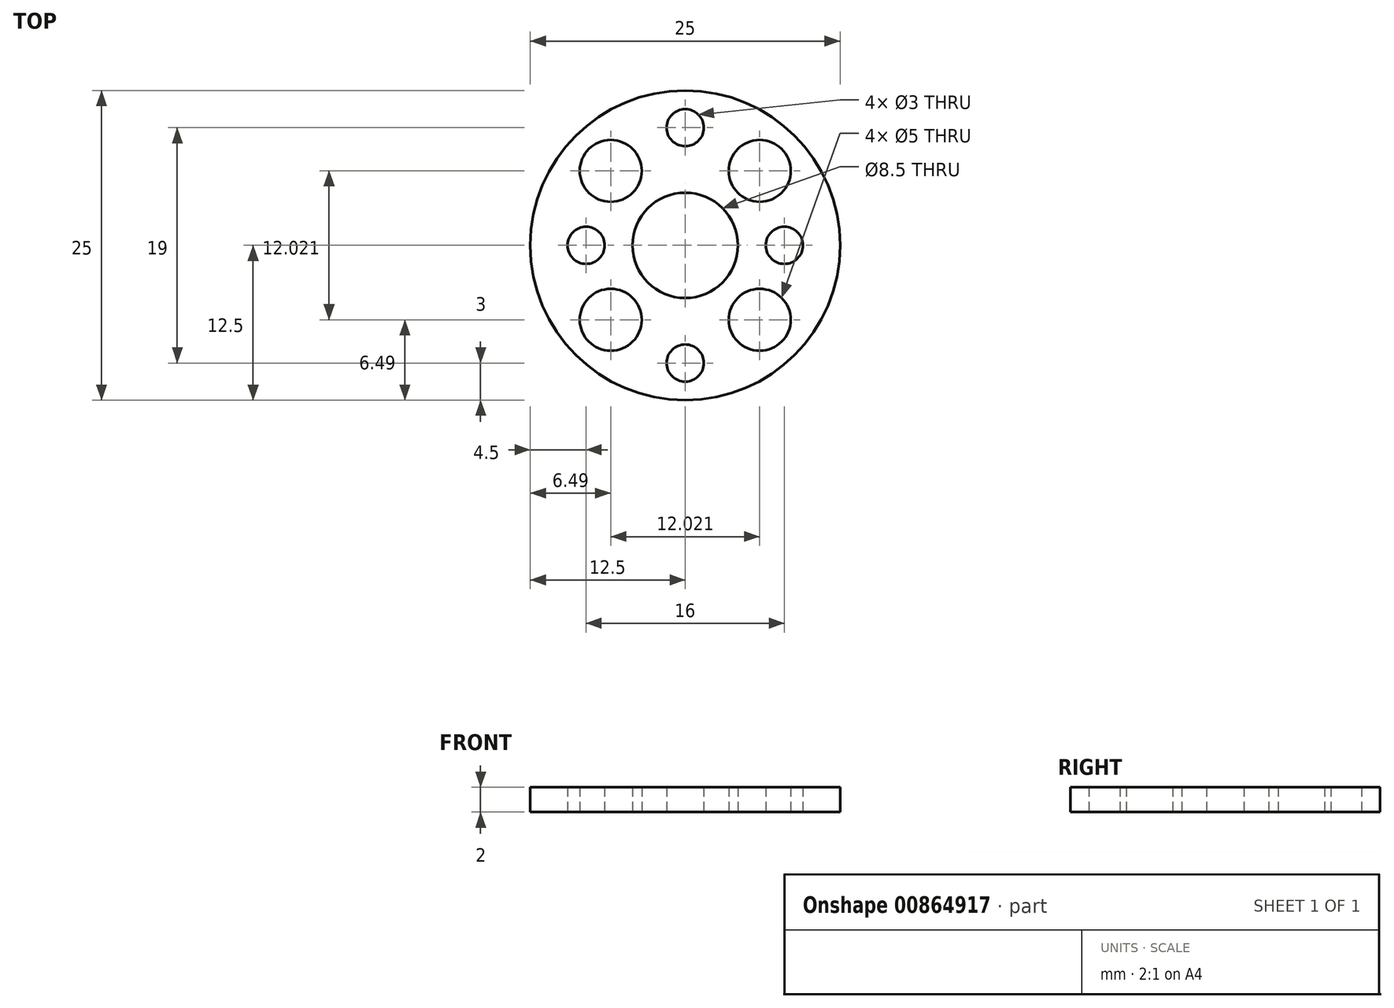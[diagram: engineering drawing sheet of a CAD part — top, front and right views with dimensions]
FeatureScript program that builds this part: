
annotation { "Feature Type Name" : "Feature", "Feature Type Description" : "" }
export const myFeature = defineFeature(function(context is Context, id is Id, definition is map)
    precondition{}
    {
        {
            var Q0;
            Q0=qCreatedBy(makeId("Top.planeOp"),FACE);
            var sketch = newSketch(context, id + "F0", { "sketchPlane" : qUnion([Q0])});
            skCircle(sketch, "E0", {"center": v(0, 0) * mm, "radius": 12.5 * mm});
            skCircle(sketch, "E1", {"center": v(0, 0) * mm, "radius": 4.25 * mm});
            skCircle(sketch, "E2", {"center": v(0, 9.5) * mm, "radius": 1.5 * mm});
            skCircle(sketch, "E3.2.0", {"center": v(0, -9.5) * mm, "radius": 1.5 * mm});
            skLineSegment(sketch, "E3.anchor1", {"start": v(0, 0) * mm, "end": v(0, 9.5) * mm, "construction": true});
            skLineSegment(sketch, "E3.anchor2", {"start": v(0, 0) * mm, "end": v(0, -9.5) * mm, "construction": true});
            skCircle(sketch, "E4", {"center": v(8, 0) * mm, "radius": 1.5 * mm});
            skCircle(sketch, "E5.2.0", {"center": v(-8, 0) * mm, "radius": 1.5 * mm});
            skLineSegment(sketch, "E5.anchor1", {"start": v(0, 0) * mm, "end": v(8, 0) * mm, "construction": true});
            skLineSegment(sketch, "E5.anchor2", {"start": v(0, 0) * mm, "end": v(-8, 0) * mm, "construction": true});
            skCircle(sketch, "E6.1.0", {"center": v(6.01, 6.01) * mm, "radius": 2.5 * mm});
            skLineSegment(sketch, "E6.anchor1", {"start": v(0, 0) * mm, "end": v(0, 8.5) * mm, "construction": true});
            skLineSegment(sketch, "E6.anchor2", {"start": v(0, 0) * mm, "end": v(8.5, 0) * mm, "construction": true});
            skCircle(sketch, "E7.1.0", {"center": v(6.01, -6.01) * mm, "radius": 2.5 * mm});
            skCircle(sketch, "E7.2.0", {"center": v(-6.01, -6.01) * mm, "radius": 2.5 * mm});
            skLineSegment(sketch, "E7.anchor1", {"start": v(0, 0) * mm, "end": v(6.01, 6.01) * mm, "construction": true});
            skLineSegment(sketch, "E7.anchor2", {"start": v(0, 0) * mm, "end": v(-6.01, -6.01) * mm, "construction": true});
            skCircle(sketch, "E8.2.0", {"center": v(-6.01, 6.01) * mm, "radius": 2.5 * mm});
            skLineSegment(sketch, "E8.anchor2", {"start": v(0, 0) * mm, "end": v(-6.01, 6.01) * mm, "construction": true});
            skSolve(sketch);
        }
        {
            var Q0;
            Q0=makeQuery(id+"F0.imprint","IMPRINT",FACE,{"disambiguationData":[TD([[makeQuery(id+"F0.imprint","IMPRINT",EDGE,{"derivedFrom":sQuery(id+"F0.wireOp",EDGE,"E0")}),1.0]])]});
            extrude(context, id + "F1", {"entities" : qUnion([Q0]), "depth" : 2 * mm, "offsetDistance" : 25 * mm});
        }
    });
